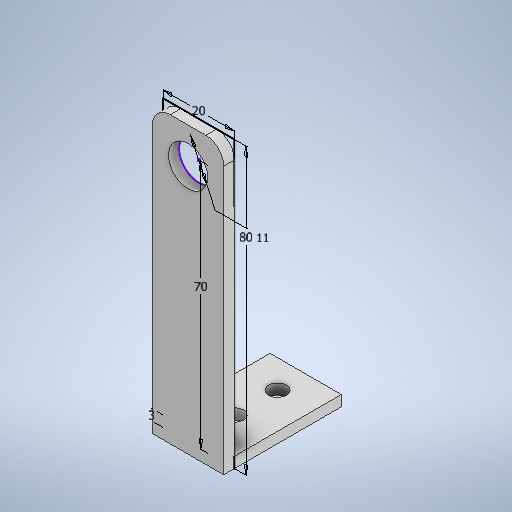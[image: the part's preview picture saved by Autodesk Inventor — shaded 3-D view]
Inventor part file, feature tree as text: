
AUTODESK INVENTOR PART (.ipt)
format: ipt  version: 2025.1 (Build 291241020, 241B)  size: 275,968 bytes
history: native  units: mm
features: extrude x5, sketch x2, fillet x1
ambient origin geometry x8: Origin, YZ Plane, XZ Plane, XY Plane, X Axis, Y Axis, Z Axis, Center Point
bodies: Solid1 (feature_tree)
feature tree (8):
  sketch  "Sketch1"  dims[d0=20.0mm d1=80.0mm d2=11.0mm]
  extrude  "Extrusion1"  Depth=80.0mm
  fillet  "Fillet1"  Radius=11.0mm
  extrude  "Extrusion2"  Depth=3.0mm TaperAngle=0.0deg
  extrude  "Extrusion3"  Depth=5.0mm
  extrude  "Extrusion4"  Depth=3.0mm
  extrude  "Extrusion5"  Depth=30.0mm TaperAngle=0.0deg
  sketch  "Sketch2"  dims[d3=70.0mm d4=3.0mm d5=0.0mm d6=5.0mm d7=3.0mm d8=30.0mm d9=0.0mm d10=5.0mm d11=5.0mm d12=0.0mm d13=0.0mm d14=10.0mm d15=0.0mm d16=10.0mm d17=0.0mm]
